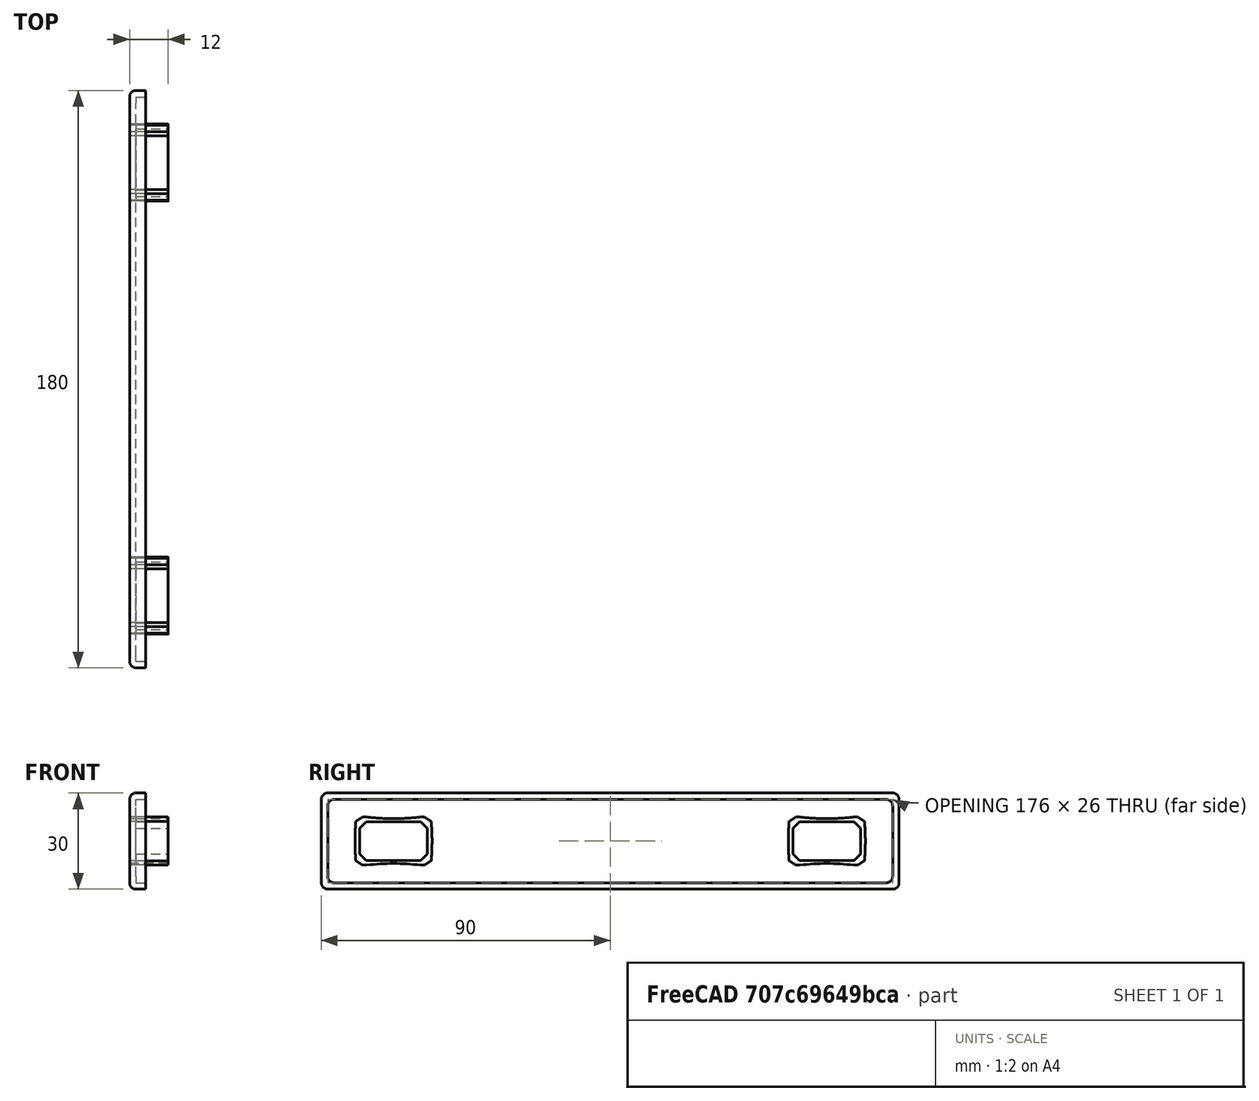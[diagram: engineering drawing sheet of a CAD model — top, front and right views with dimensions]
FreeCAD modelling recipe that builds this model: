
FCSTD DOCUMENT  (FreeCAD 1.0R39109 (Git))
Label: Transport_Handle_Cover
License: All rights reserved
LicenseURL: https://en.wikipedia.org/wiki/All_rights_reserved
objects: Part::Cylinder×40, Part::Cut×30, Part::Box×12, Part::Sphere×8, Part::MultiCommon×8, Part::Fillet×4, Part::MultiFuse×2, App::Part×2, Part::Chamfer×2
note: 106 computed .brp shape members not serialized (recipe doc carries the construction recipe); baked Part::Feature solids carry a one-line shape summary decoded from their .brp

FEATURE [Part::Box] Box  label="Cube001"
  AttacherType = Attacher::AttachEngine3D
  Height = 26
  Length = 2
  Placement = pos=(0,2,2) rot=(0,0,1;0rad)
  Width = 176
FEATURE [Part::Cylinder] Cylinder  label="Cylinder001"
  Angle = 360
  AttacherType = Attacher::AttachEngine3D
  FirstAngle = 0
  Height = 26
  Placement = pos=(2,2,2) rot=(0,0,1;1.5708rad)
  Radius = 2
  SecondAngle = 0
FEATURE [Part::Cylinder] Cylinder001  label="Cylinder002"
  Angle = 360
  AttacherType = Attacher::AttachEngine3D
  FirstAngle = 0
  Height = 26
  Placement = pos=(2,178,2) rot=(0,0,1;1.5708rad)
  Radius = 2
  SecondAngle = 0
FEATURE [Part::Cylinder] Cylinder002  label="Cylinder003"
  Angle = 360
  AttacherType = Attacher::AttachEngine3D
  FirstAngle = 0
  Height = 176
  Placement = pos=(2,178,2) rot=(1,0,0;1.5708rad)
  Radius = 2
  SecondAngle = 0
FEATURE [Part::Cylinder] Cylinder003  label="Cylinder004"
  Angle = 360
  AttacherType = Attacher::AttachEngine3D
  FirstAngle = 0
  Height = 176
  Placement = pos=(2,178,28) rot=(1,0,0;1.5708rad)
  Radius = 2
  SecondAngle = 0
FEATURE [Part::Box] Box001  label="Cube002"
  AttacherType = Attacher::AttachEngine3D
  Height = 30
  Length = 3
  Placement = pos=(2,0,0) rot=(0,0,1;0rad)
  Width = 180
FEATURE [Part::Sphere] Sphere  label="Sphere001"
  Angle1 = -90
  Angle2 = 90
  Angle3 = 360
  AttacherType = Attacher::AttachEngine3D
  Placement = pos=(2,2,2) rot=(0,0,1;0rad)
  Radius = 2
FEATURE [Part::Sphere] Sphere001  label="Sphere002"
  Angle1 = -90
  Angle2 = 90
  Angle3 = 360
  AttacherType = Attacher::AttachEngine3D
  Placement = pos=(2,178,2) rot=(0,0,1;0rad)
  Radius = 2
FEATURE [Part::Sphere] Sphere002  label="Sphere003"
  Angle1 = -90
  Angle2 = 90
  Angle3 = 360
  AttacherType = Attacher::AttachEngine3D
  Placement = pos=(2,2,28) rot=(0,0,1;0rad)
  Radius = 2
FEATURE [Part::Sphere] Sphere003  label="Sphere004"
  Angle1 = -90
  Angle2 = 90
  Angle3 = 360
  AttacherType = Attacher::AttachEngine3D
  Placement = pos=(2,178,28) rot=(0,0,1;0rad)
  Radius = 2
FEATURE [Part::Fillet] Fillet
  Base = -> Box001
  EdgeLinks = -> Box001 [Edge9,Edge10,Edge11,Edge12]
  Edges = 4 edges r=2: [Edge9,Edge10,Edge11,Edge12]
FEATURE [Part::Box] Box002  label="Cube003"
  AttacherType = Attacher::AttachEngine3D
  Height = 26
  Length = 3
  Placement = pos=(7,2,2) rot=(0,0,1;0rad)
  Width = 176
FEATURE [Part::Fillet] Fillet001
  Base = -> Box002
  EdgeLinks = -> Box002 [Edge9,Edge10,Edge11,Edge12]
  Edges = 4 edges r=2: [Edge9,Edge10,Edge11,Edge12]
  Placement = pos=(-5,0,0) rot=(0,0,1;0rad)
FEATURE [Part::MultiFuse] Fusion
  Shapes = -> [Fillet,Box,Cylinder,Cylinder001,Cylinder002,Cylinder003,Sphere,Sphere001,Sphere002,Sphere003]
FEATURE [Part::Box] Box003  label="Cube"
  AttacherType = Attacher::AttachEngine3D
  Height = 15
  Length = 10
  Placement = pos=(22,-12,0) rot=(0,0,1;0rad)
  Width = 24
FEATURE [Part::Cylinder] Cylinder004  label="Cylinder"
  Angle = 360
  AttacherType = Attacher::AttachEngine3D
  FirstAngle = 0
  Height = 10
  Placement = pos=(22,0,-69.5) rot=(0,1,0;1.5708rad)
  Radius = 70
  SecondAngle = 0
FEATURE [Part::Cylinder] Cylinder005
  Angle = 360
  AttacherType = Attacher::AttachEngine3D
  FirstAngle = 0
  Height = 10
  Placement = pos=(22,0,84.5) rot=(0,1,0;1.5708rad)
  Radius = 70
  SecondAngle = 0
FEATURE [Part::Cut] Cut
  Base = -> Box003
  Tool = -> Cylinder004
FEATURE [Part::Cylinder] Cylinder006
  Angle = 360
  AttacherType = Attacher::AttachEngine3D
  FirstAngle = 0
  Height = 10
  Placement = pos=(22,58,7.5) rot=(0,1,0;1.5708rad)
  Radius = 70
  SecondAngle = 0
FEATURE [Part::Cylinder] Cylinder008
  Angle = 360
  AttacherType = Attacher::AttachEngine3D
  FirstAngle = 0
  Height = 10
  Placement = pos=(22,27,39.5) rot=(0,1,0;1.5708rad)
  Radius = 30
  SecondAngle = 0
FEATURE [Part::Cut] Cut001
  Base = -> Cut
  Tool = -> Cylinder005
FEATURE [Part::Cylinder] Cylinder009
  Angle = 360
  AttacherType = Attacher::AttachEngine3D
  FirstAngle = 0
  Height = 10
  Placement = pos=(22,-58,7.5) rot=(0,1,0;1.5708rad)
  Radius = 70
  SecondAngle = 0
FEATURE [Part::MultiCommon] Common
  Shapes = -> [Cut001,Cylinder006]
FEATURE [Part::MultiCommon] Common001
  Shapes = -> [Common,Cylinder009]
FEATURE [Part::Cylinder] Cylinder010
  Angle = 360
  AttacherType = Attacher::AttachEngine3D
  FirstAngle = 0
  Height = 10
  Placement = pos=(22,27,-24.5) rot=(0,1,0;1.5708rad)
  Radius = 30
  SecondAngle = 0
FEATURE [Part::Cut] Cut002
  Base = -> Common001
  Tool = -> Cylinder008
FEATURE [Part::Cylinder] Cylinder011
  Angle = 360
  AttacherType = Attacher::AttachEngine3D
  FirstAngle = 0
  Height = 10
  Placement = pos=(22,-27,-24.5) rot=(0,1,0;1.5708rad)
  Radius = 30
  SecondAngle = 0
FEATURE [Part::Cut] Cut003
  Base = -> Cut002
  Tool = -> Cylinder010
FEATURE [Part::Cylinder] Cylinder012
  Angle = 360
  AttacherType = Attacher::AttachEngine3D
  FirstAngle = 0
  Height = 10
  Placement = pos=(22,-27,39.5) rot=(0,1,0;1.5708rad)
  Radius = 30
  SecondAngle = 0
FEATURE [Part::Cut] Cut004
  Base = -> Cut003
  Tool = -> Cylinder011
FEATURE [Part::Cut] Cut005
  Base = -> Cut004
  Placement = pos=(-25,157.5,7.5) rot=(0,0,1;0rad)
  Tool = -> Cylinder012
FEATURE [Part::Box] Box004  label="Cube004"
  AttacherType = Attacher::AttachEngine3D
  Height = 15
  Length = 10
  Placement = pos=(22,-12,0) rot=(0,0,1;0rad)
  Width = 24
FEATURE [Part::Cylinder] Cylinder013
  Angle = 360
  AttacherType = Attacher::AttachEngine3D
  FirstAngle = 0
  Height = 10
  Placement = pos=(22,0,-69.5) rot=(0,1,0;1.5708rad)
  Radius = 70
  SecondAngle = 0
FEATURE [Part::Cut] Cut006
  Base = -> Box004
  Tool = -> Cylinder013
FEATURE [Part::Cylinder] Cylinder014
  Angle = 360
  AttacherType = Attacher::AttachEngine3D
  FirstAngle = 0
  Height = 10
  Placement = pos=(22,0,84.5) rot=(0,1,0;1.5708rad)
  Radius = 70
  SecondAngle = 0
FEATURE [Part::Cut] Cut007
  Base = -> Cut006
  Tool = -> Cylinder014
FEATURE [Part::Cylinder] Cylinder015
  Angle = 360
  AttacherType = Attacher::AttachEngine3D
  FirstAngle = 0
  Height = 10
  Placement = pos=(22,58,7.5) rot=(0,1,0;1.5708rad)
  Radius = 70
  SecondAngle = 0
FEATURE [Part::MultiCommon] Common002
  Shapes = -> [Cut007,Cylinder015]
FEATURE [Part::Cylinder] Cylinder016
  Angle = 360
  AttacherType = Attacher::AttachEngine3D
  FirstAngle = 0
  Height = 10
  Placement = pos=(22,27,39.5) rot=(0,1,0;1.5708rad)
  Radius = 30
  SecondAngle = 0
FEATURE [Part::Cylinder] Cylinder017
  Angle = 360
  AttacherType = Attacher::AttachEngine3D
  FirstAngle = 0
  Height = 10
  Placement = pos=(22,-58,7.5) rot=(0,1,0;1.5708rad)
  Radius = 70
  SecondAngle = 0
FEATURE [Part::MultiCommon] Common003
  Shapes = -> [Common002,Cylinder017]
FEATURE [Part::Cut] Cut008
  Base = -> Common003
  Tool = -> Cylinder016
FEATURE [Part::Cylinder] Cylinder018
  Angle = 360
  AttacherType = Attacher::AttachEngine3D
  FirstAngle = 0
  Height = 10
  Placement = pos=(22,27,-24.5) rot=(0,1,0;1.5708rad)
  Radius = 30
  SecondAngle = 0
FEATURE [Part::Cut] Cut009
  Base = -> Cut008
  Tool = -> Cylinder018
FEATURE [Part::Cylinder] Cylinder019
  Angle = 360
  AttacherType = Attacher::AttachEngine3D
  FirstAngle = 0
  Height = 10
  Placement = pos=(22,-27,-24.5) rot=(0,1,0;1.5708rad)
  Radius = 30
  SecondAngle = 0
FEATURE [Part::Cut] Cut010
  Base = -> Cut009
  Tool = -> Cylinder019
FEATURE [Part::Cylinder] Cylinder020
  Angle = 360
  AttacherType = Attacher::AttachEngine3D
  FirstAngle = 0
  Height = 10
  Placement = pos=(22,-27,39.5) rot=(0,1,0;1.5708rad)
  Radius = 30
  SecondAngle = 0
FEATURE [Part::Cut] Cut011
  Base = -> Cut010
  Placement = pos=(-25,22.5,7.5) rot=(0,0,1;0rad)
  Tool = -> Cylinder020
FEATURE [Part::Cut] Cut012
  Base = -> Fusion
  Tool = -> Cut005
FEATURE [Part::Cut] Cut013
  Base = -> Cut012
  Tool = -> Cut011
FEATURE [Part::Cut] Cut014
  Base = -> Cut013
  Tool = -> Fillet001
FEATURE [App::Part] Part  label="v1"
  Group = -> [Box,Cylinder001,Cylinder,Cylinder002,Cylinder003,Box001,Sphere,Sphere001,Sphere002,Sphere003,Fillet,Box002,Fillet001,Fusion,Box003,Cylinder004,Cylinder005,Cut,Cylinder006,Cylinder008,Cut001,Cylinder009,Common,Common001,Cylinder010,Cut002,Cylinder011,Cut003,Cylinder012,Cut004,Cut005,Box004,Common002,Common003,Cut006,Cut007,Cut008,Cut009,Cut010,Cut011,Cylinder013,Cylinder014,Cylinder015,Cylinder016,+7 more]
  Origin = -> Origin
  Placement = pos=(-17,0,0) rot=(0,0,1;0rad)
FEATURE [Part::Box] Box005  label="Cube005"
  AttacherType = Attacher::AttachEngine3D
  Height = 26
  Length = 2
  Placement = pos=(0,2,2) rot=(0,0,1;0rad)
  Width = 176
FEATURE [Part::Box] Box006  label="Cube006"
  AttacherType = Attacher::AttachEngine3D
  Height = 30
  Length = 3
  Placement = pos=(2,0,0) rot=(0,0,1;0rad)
  Width = 180
FEATURE [Part::Box] Box007  label="Cube007"
  AttacherType = Attacher::AttachEngine3D
  Height = 26
  Length = 3
  Placement = pos=(7,2,2) rot=(0,0,1;0rad)
  Width = 176
FEATURE [Part::Box] Box008  label="Cube008"
  AttacherType = Attacher::AttachEngine3D
  Height = 15
  Length = 10
  Placement = pos=(22,-12,0) rot=(0,0,1;0rad)
  Width = 24
FEATURE [Part::Box] Box009  label="Cube009"
  AttacherType = Attacher::AttachEngine3D
  Height = 15
  Length = 10
  Placement = pos=(22,-12,0) rot=(0,0,1;0rad)
  Width = 24
FEATURE [Part::Cylinder] Cylinder021
  Angle = 360
  AttacherType = Attacher::AttachEngine3D
  FirstAngle = 0
  Height = 26
  Placement = pos=(2,2,2) rot=(0,0,1;1.5708rad)
  Radius = 2
  SecondAngle = 0
FEATURE [Part::Cylinder] Cylinder022
  Angle = 360
  AttacherType = Attacher::AttachEngine3D
  FirstAngle = 0
  Height = 26
  Placement = pos=(2,178,2) rot=(0,0,1;1.5708rad)
  Radius = 2
  SecondAngle = 0
FEATURE [Part::Cylinder] Cylinder023
  Angle = 360
  AttacherType = Attacher::AttachEngine3D
  FirstAngle = 0
  Height = 176
  Placement = pos=(2,178,2) rot=(1,0,0;1.5708rad)
  Radius = 2
  SecondAngle = 0
FEATURE [Part::Cylinder] Cylinder024
  Angle = 360
  AttacherType = Attacher::AttachEngine3D
  FirstAngle = 0
  Height = 176
  Placement = pos=(2,178,28) rot=(1,0,0;1.5708rad)
  Radius = 2
  SecondAngle = 0
FEATURE [Part::Cylinder] Cylinder025
  Angle = 360
  AttacherType = Attacher::AttachEngine3D
  FirstAngle = 0
  Height = 10
  Placement = pos=(22,0,-69.5) rot=(0,1,0;1.5708rad)
  Radius = 70
  SecondAngle = 0
FEATURE [Part::Cut] Cut015
  Base = -> Box008
  Tool = -> Cylinder025
FEATURE [Part::Cylinder] Cylinder026
  Angle = 360
  AttacherType = Attacher::AttachEngine3D
  FirstAngle = 0
  Height = 10
  Placement = pos=(22,0,84.5) rot=(0,1,0;1.5708rad)
  Radius = 70
  SecondAngle = 0
FEATURE [Part::Cut] Cut016
  Base = -> Cut015
  Tool = -> Cylinder026
FEATURE [Part::Cylinder] Cylinder027
  Angle = 360
  AttacherType = Attacher::AttachEngine3D
  FirstAngle = 0
  Height = 10
  Placement = pos=(22,58,7.5) rot=(0,1,0;1.5708rad)
  Radius = 70
  SecondAngle = 0
FEATURE [Part::MultiCommon] Common004
  Shapes = -> [Cut016,Cylinder027]
FEATURE [Part::Cylinder] Cylinder028
  Angle = 360
  AttacherType = Attacher::AttachEngine3D
  FirstAngle = 0
  Height = 10
  Placement = pos=(22,27,39.5) rot=(0,1,0;1.5708rad)
  Radius = 30
  SecondAngle = 0
FEATURE [Part::Cylinder] Cylinder029
  Angle = 360
  AttacherType = Attacher::AttachEngine3D
  FirstAngle = 0
  Height = 10
  Placement = pos=(22,-58,7.5) rot=(0,1,0;1.5708rad)
  Radius = 70
  SecondAngle = 0
FEATURE [Part::MultiCommon] Common005
  Shapes = -> [Common004,Cylinder029]
FEATURE [Part::Cut] Cut017
  Base = -> Common005
  Tool = -> Cylinder028
FEATURE [Part::Cylinder] Cylinder030
  Angle = 360
  AttacherType = Attacher::AttachEngine3D
  FirstAngle = 0
  Height = 10
  Placement = pos=(22,27,-24.5) rot=(0,1,0;1.5708rad)
  Radius = 30
  SecondAngle = 0
FEATURE [Part::Cut] Cut018
  Base = -> Cut017
  Tool = -> Cylinder030
FEATURE [Part::Cylinder] Cylinder031
  Angle = 360
  AttacherType = Attacher::AttachEngine3D
  FirstAngle = 0
  Height = 10
  Placement = pos=(22,-27,-24.5) rot=(0,1,0;1.5708rad)
  Radius = 30
  SecondAngle = 0
FEATURE [Part::Cut] Cut019
  Base = -> Cut018
  Tool = -> Cylinder031
FEATURE [Part::Cylinder] Cylinder032
  Angle = 360
  AttacherType = Attacher::AttachEngine3D
  FirstAngle = 0
  Height = 10
  Placement = pos=(22,-27,39.5) rot=(0,1,0;1.5708rad)
  Radius = 30
  SecondAngle = 0
FEATURE [Part::Cut] Cut020
  Base = -> Cut019
  Placement = pos=(-20,157.5,7.5) rot=(0,0,1;0rad)
  Tool = -> Cylinder032
FEATURE [Part::Cylinder] Cylinder033
  Angle = 360
  AttacherType = Attacher::AttachEngine3D
  FirstAngle = 0
  Height = 10
  Placement = pos=(22,0,-69.5) rot=(0,1,0;1.5708rad)
  Radius = 70
  SecondAngle = 0
FEATURE [Part::Cut] Cut021
  Base = -> Box009
  Tool = -> Cylinder033
FEATURE [Part::Cylinder] Cylinder034
  Angle = 360
  AttacherType = Attacher::AttachEngine3D
  FirstAngle = 0
  Height = 10
  Placement = pos=(22,0,84.5) rot=(0,1,0;1.5708rad)
  Radius = 70
  SecondAngle = 0
FEATURE [Part::Cut] Cut022
  Base = -> Cut021
  Tool = -> Cylinder034
FEATURE [Part::Cylinder] Cylinder035
  Angle = 360
  AttacherType = Attacher::AttachEngine3D
  FirstAngle = 0
  Height = 10
  Placement = pos=(22,58,7.5) rot=(0,1,0;1.5708rad)
  Radius = 70
  SecondAngle = 0
FEATURE [Part::MultiCommon] Common006
  Shapes = -> [Cut022,Cylinder035]
FEATURE [Part::Cylinder] Cylinder036
  Angle = 360
  AttacherType = Attacher::AttachEngine3D
  FirstAngle = 0
  Height = 10
  Placement = pos=(22,27,39.5) rot=(0,1,0;1.5708rad)
  Radius = 30
  SecondAngle = 0
FEATURE [Part::Cylinder] Cylinder037
  Angle = 360
  AttacherType = Attacher::AttachEngine3D
  FirstAngle = 0
  Height = 10
  Placement = pos=(22,-58,7.5) rot=(0,1,0;1.5708rad)
  Radius = 70
  SecondAngle = 0
FEATURE [Part::MultiCommon] Common007
  Shapes = -> [Common006,Cylinder037]
FEATURE [Part::Cut] Cut023
  Base = -> Common007
  Tool = -> Cylinder036
FEATURE [Part::Cylinder] Cylinder038
  Angle = 360
  AttacherType = Attacher::AttachEngine3D
  FirstAngle = 0
  Height = 10
  Placement = pos=(22,27,-24.5) rot=(0,1,0;1.5708rad)
  Radius = 30
  SecondAngle = 0
FEATURE [Part::Cut] Cut024
  Base = -> Cut023
  Tool = -> Cylinder038
FEATURE [Part::Cylinder] Cylinder039
  Angle = 360
  AttacherType = Attacher::AttachEngine3D
  FirstAngle = 0
  Height = 10
  Placement = pos=(22,-27,-24.5) rot=(0,1,0;1.5708rad)
  Radius = 30
  SecondAngle = 0
FEATURE [Part::Cut] Cut025
  Base = -> Cut024
  Tool = -> Cylinder039
FEATURE [Part::Cylinder] Cylinder040
  Angle = 360
  AttacherType = Attacher::AttachEngine3D
  FirstAngle = 0
  Height = 10
  Placement = pos=(22,-27,39.5) rot=(0,1,0;1.5708rad)
  Radius = 30
  SecondAngle = 0
FEATURE [Part::Cut] Cut026
  Base = -> Cut025
  Placement = pos=(-20,22.5,7.5) rot=(0,0,1;0rad)
  Tool = -> Cylinder040
FEATURE [Part::Fillet] Fillet002
  Base = -> Box006
  EdgeLinks = -> Box006 [Edge9,Edge10,Edge11,Edge12]
  Edges = 4 edges r=2: [Edge9,Edge10,Edge11,Edge12]
FEATURE [Part::Fillet] Fillet003
  Base = -> Box007
  EdgeLinks = -> Box007 [Edge9,Edge10,Edge11,Edge12]
  Edges = 4 edges r=2: [Edge9,Edge10,Edge11,Edge12]
  Placement = pos=(-5,0,0) rot=(0,0,1;0rad)
FEATURE [Part::Sphere] Sphere004  label="Sphere005"
  Angle1 = -90
  Angle2 = 90
  Angle3 = 360
  AttacherType = Attacher::AttachEngine3D
  Placement = pos=(2,2,2) rot=(0,0,1;0rad)
  Radius = 2
FEATURE [Part::Sphere] Sphere005  label="Sphere006"
  Angle1 = -90
  Angle2 = 90
  Angle3 = 360
  AttacherType = Attacher::AttachEngine3D
  Placement = pos=(2,178,2) rot=(0,0,1;0rad)
  Radius = 2
FEATURE [Part::Sphere] Sphere006  label="Sphere007"
  Angle1 = -90
  Angle2 = 90
  Angle3 = 360
  AttacherType = Attacher::AttachEngine3D
  Placement = pos=(2,2,28) rot=(0,0,1;0rad)
  Radius = 2
FEATURE [Part::Sphere] Sphere007  label="Sphere008"
  Angle1 = -90
  Angle2 = 90
  Angle3 = 360
  AttacherType = Attacher::AttachEngine3D
  Placement = pos=(2,178,28) rot=(0,0,1;0rad)
  Radius = 2
FEATURE [Part::MultiFuse] Fusion001
  Shapes = -> [Fillet002,Box005,Cylinder021,Cylinder022,Cylinder023,Cylinder024,Sphere004,Sphere005,Sphere006,Sphere007]
FEATURE [Part::Cut] Cut027
  Base = -> Fusion001
  Tool = -> Fillet003
FEATURE [Part::Box] Box010  label="Cube010"
  AttacherType = Attacher::AttachEngine3D
  Height = 12
  Length = 10
  Placement = pos=(2,12,9) rot=(0,0,1;0rad)
  Width = 21
FEATURE [Part::Chamfer] Chamfer
  Base = -> Box010
  EdgeLinks = -> Box010 [Edge9,Edge10,Edge11,Edge12]
  Edges = 4 edges r=2: [Edge9,Edge10,Edge11,Edge12]
FEATURE [Part::Box] Box011  label="Cube011"
  AttacherType = Attacher::AttachEngine3D
  Height = 12
  Length = 10
  Placement = pos=(2,12,9) rot=(0,0,1;0rad)
  Width = 21
FEATURE [Part::Chamfer] Chamfer001
  Base = -> Box011
  EdgeLinks = -> Box011 [Edge9,Edge10,Edge11,Edge12]
  Edges = 4 edges r=2: [Edge9,Edge10,Edge11,Edge12]
  Placement = pos=(0,135,0) rot=(0,0,1;0rad)
FEATURE [Part::Cut] Cut028
  Base = -> Cut026
  Tool = -> Chamfer
FEATURE [Part::Cut] Cut029
  Base = -> Cut020
  Tool = -> Chamfer001
FEATURE [App::Part] Part001  label="v2"
  Group = -> [Box005,Box006,Box007,Cylinder021,Cylinder022,Cylinder023,Cylinder024,Fillet002,Fillet003,Fusion001,Sphere004,Sphere005,Sphere006,Sphere007,Cut027,Chamfer,Box009,Common006,Common007,Cut021,Cut022,Cut023,Cut024,Cut025,Cut026,Cylinder033,Cylinder034,Cylinder035,Cylinder036,Cylinder037,Cylinder038,Cylinder039,Cylinder040,Box010,Cut028,Common005,Common004,Box008,Cut015,Cut016,Cut017,Cut018,Cut019,+12 more]
  Origin = -> Origin001
